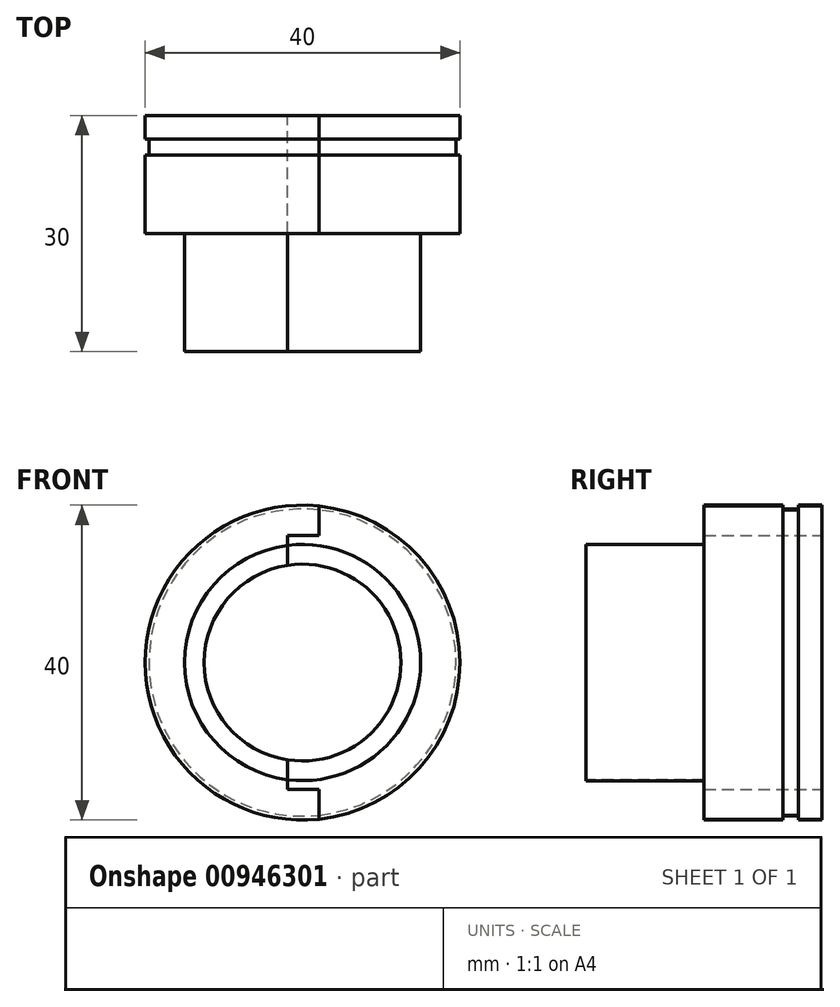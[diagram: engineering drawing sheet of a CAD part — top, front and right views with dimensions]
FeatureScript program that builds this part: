
annotation { "Feature Type Name" : "Feature", "Feature Type Description" : "" }
export const myFeature = defineFeature(function(context is Context, id is Id, definition is map)
    precondition{}
    {
        {
            var Q0;
            Q0=qCreatedBy(makeId("Front.planeOp"),FACE);
            var sketch = newSketch(context, id + "F0", { "sketchPlane" : qUnion([Q0])});
            skCircle(sketch, "E0", {"center": v(0, 0) * mm, "radius": 12.5 * mm});
            skCircle(sketch, "E1", {"center": v(0, 0) * mm, "radius": 15 * mm});
            skCircle(sketch, "E2", {"center": v(0, 0) * mm, "radius": 20 * mm});
            skSolve(sketch);
        }
        {
            var Q0;
            Q0=makeQuery(id+"F0.imprint","IMPRINT",FACE,{"disambiguationData":[TD([[makeQuery(id+"F0.imprint","IMPRINT",EDGE,{"derivedFrom":sQuery(id+"F0.wireOp",EDGE,"E0")}),-1.0]])]});
            extrude(context, id + "F1", {"entities" : qUnion([Q0]), "depth" : 30 * mm, "offsetDistance" : 25 * mm});
        }
        {
            var Q0;
            Q0 = qSketchRegion(id + "F0", true);
            extrude(context, id + "F2", {"entities" : qUnion([Q0]), "operationType" : NewBodyOperationType.ADD, "depth" : 30 * mm, "offsetDistance" : 25 * mm});
        }
        {
            var Q0;
            {var subQ0=sQuery(id+"F0.wireOp",EDGE,"E1");Q0=makeQuery(id+"F2.boolean.opBoolean","MERGE",FACE,{"derivedFrom":[makeQuery(id+"F1.opExtrude","CAP_FACE",FACE,{"disambiguationData":[OSD([sQuery(id+"F0.wireOp",EDGE,"E0"),subQ0])],"isStart":true}),makeQuery(id+"F2.opExtrude","CAP_FACE",FACE,{"disambiguationData":[OSD([subQ0,sQuery(id+"F0.wireOp",EDGE,"E2")])],"isStart":true})]});}
            var sketch = newSketch(context, id + "F3", { "sketchPlane" : qUnion([Q0])});
            skLineSegment(sketch, "E3", {"start": v(0, 27.45) * mm, "end": v(0, -30.32) * mm, "construction": true});
            skLineSegment(sketch, "E4", {"start": v(-35.74, 0) * mm, "end": v(39.77, 0) * mm, "construction": true});
            skLineSegment(sketch, "E5", {"start": v(-2.08, 19.9) * mm, "end": v(-2.08, 16.12) * mm});
            skLineSegment(sketch, "E6", {"start": v(-2.08, 16.12) * mm, "end": v(1.92, 16.12) * mm});
            skLineSegment(sketch, "E7", {"start": v(1.92, 16.12) * mm, "end": v(1.92, 12.35) * mm});
            skLineSegment(sketch, "E8.MirrorCS", {"start": v(1.92, -16.12) * mm, "end": v(1.92, -12.35) * mm});
            skLineSegment(sketch, "E9.MirrorCS", {"start": v(-2.08, -19.9) * mm, "end": v(-2.08, -16.12) * mm});
            skLineSegment(sketch, "E10.MirrorCS", {"start": v(-2.08, -16.12) * mm, "end": v(1.92, -16.12) * mm});
            skSolve(sketch);
        }
        {
            var Q0;
            {var subQ2=sQuery(id+"F3.wireOp",EDGE,"E5");Q0=makeQuery(id+"F3.imprint","IMPRINT",FACE,{"disambiguationData":[TD([[makeQuery(id+"F3.imprint","IMPRINT",EDGE,{"derivedFrom":subQ2}),-1.0]])]});}
            var sketch = newSketch(context, id + "F4", { "sketchPlane" : qUnion([Q0])});
            skLineSegment(sketch, "E11", {"start": v(-19.9, -2) * mm, "end": v(-15.9, -2) * mm});
            skLineSegment(sketch, "E12", {"start": v(-15.9, -2) * mm, "end": v(-15.9, 2) * mm});
            skLineSegment(sketch, "E13", {"start": v(-15.9, 2) * mm, "end": v(-12.34, 2) * mm});
            skLineSegment(sketch, "E14", {"start": v(-12.34, 1.9) * mm, "end": v(-15.84, 1.9) * mm});
            skLineSegment(sketch, "E15", {"start": v(-15.84, 1.9) * mm, "end": v(-15.84, -2.1) * mm});
            skLineSegment(sketch, "E16", {"start": v(-15.84, -2.1) * mm, "end": v(-19.84, -2.1) * mm});
            skSolve(sketch);
        }
        {
            var Q0;
            {var subQ3=sQuery(id+"F4.wireOp",EDGE,"E11");Q0=makeQuery(id+"F4.imprint","IMPRINT",FACE,{"disambiguationData":[TD([[makeQuery(id+"F4.imprint","IMPRINT",EDGE,{"derivedFrom":subQ3}),1.0]])]});}
            var Q1;
            {var subQ7=sQuery(id+"F4.wireOp",EDGE,"E11");Q1=makeQuery(id+"F4.imprint","IMPRINT",FACE,{"disambiguationData":[TD([[makeQuery(id+"F4.imprint","IMPRINT",EDGE,{"derivedFrom":subQ7}),-1.0]])]});}
            extrude(context, id + "F5", {"entities" : qUnion([Q0, Q1]), "operationType" : NewBodyOperationType.REMOVE, "endBound" : BoundingType.THROUGH_ALL, "oppositeDirection" : true, "depth" : 25 * mm, "offsetDistance" : 25 * mm});
        }
        {
            var Q0;
            {var subQ2=sQuery(id+"F3.wireOp",EDGE,"E5");Q0=makeQuery(id+"F3.imprint","IMPRINT",FACE,{"disambiguationData":[TD([[makeQuery(id+"F3.imprint","IMPRINT",EDGE,{"derivedFrom":subQ2}),-1.0]])]});}
            extrude(context, id + "F6", {"entities" : qUnion([Q0]), "oppositeDirection" : true, "depth" : 30 * mm, "offsetDistance" : 25 * mm});
        }
        {
            var Q0;
            {var subQ0=sQuery(id+"F0.wireOp",EDGE,"E1");Q0=makeQuery(id+"F2.boolean.opBoolean","MERGE",FACE,{"derivedFrom":[makeQuery(id+"F1.opExtrude","CAP_FACE",FACE,{"disambiguationData":[OSD([sQuery(id+"F0.wireOp",EDGE,"E0"),subQ0])],"isStart":false}),makeQuery(id+"F2.opExtrude","CAP_FACE",FACE,{"disambiguationData":[OSD([subQ0,sQuery(id+"F0.wireOp",EDGE,"E2")])],"isStart":false})]});}
            var sketch = newSketch(context, id + "F7", { "sketchPlane" : qUnion([Q0])});
            skCircle(sketch, "E17", {"center": v(0, 0) * mm, "radius": 15 * mm});
            skSolve(sketch);
        }
        {
            var Q0;
            {var subQ0=sQuery(id+"F0.wireOp",EDGE,"E2");Q0=makeQuery(id+"F7.imprint","IMPRINT",FACE,{"disambiguationData":[TD([[makeQuery(id+"F7.imprint","IMPRINT",EDGE,{"derivedFrom":makeQuery(id+"F2.opExtrude","CAP_EDGE",EDGE,{"disambiguationData":[OSD([subQ0])],"isStart":false})}),1.0]])]});}
            extrude(context, id + "F8", {"entities" : qUnion([Q0]), "operationType" : NewBodyOperationType.REMOVE, "oppositeDirection" : true, "depth" : 15 * mm, "offsetDistance" : 25 * mm});
        }
        {
            var Q0;
            Q0=makeQuery(id+"F6.opExtrude","CAP_FACE",FACE,{"disambiguationData":[OSD([sQuery(id+"F0.wireOp",EDGE,"E0"),sQuery(id+"F0.wireOp",EDGE,"E2"),sQuery(id+"F3.wireOp",EDGE,"E5"),sQuery(id+"F3.wireOp",EDGE,"E6"),sQuery(id+"F3.wireOp",EDGE,"E7"),sQuery(id+"F3.wireOp",EDGE,"E8.MirrorCS"),sQuery(id+"F3.wireOp",EDGE,"E9.MirrorCS"),sQuery(id+"F3.wireOp",EDGE,"E10.MirrorCS")])],"isStart":false});
            var sketch = newSketch(context, id + "F9", { "sketchPlane" : qUnion([Q0])});
            skCircle(sketch, "E18", {"center": v(0, 0) * mm, "radius": 15 * mm});
            skSolve(sketch);
        }
        {
            var Q0;
            Q0=makeQuery(id+"F9.imprint","IMPRINT",FACE,{"disambiguationData":[TD([[makeQuery(id+"F9.imprint","IMPRINT",EDGE,{"derivedFrom":makeQuery(id+"F6.opExtrude","CAP_EDGE",EDGE,{"disambiguationData":[OSD([sQuery(id+"F3.wireOp",EDGE,"E5")])],"isStart":false})}),1.0]])]});
            extrude(context, id + "F10", {"entities" : qUnion([Q0]), "operationType" : NewBodyOperationType.REMOVE, "oppositeDirection" : true, "depth" : 15 * mm, "offsetDistance" : 25 * mm});
        }
        {
            var Q0;
            Q0=makeQuery(id+"F6.opExtrude","CAP_FACE",FACE,{"disambiguationData":[OSD([sQuery(id+"F0.wireOp",EDGE,"E0"),sQuery(id+"F0.wireOp",EDGE,"E2"),sQuery(id+"F3.wireOp",EDGE,"E5"),sQuery(id+"F3.wireOp",EDGE,"E6"),sQuery(id+"F3.wireOp",EDGE,"E7"),sQuery(id+"F3.wireOp",EDGE,"E8.MirrorCS"),sQuery(id+"F3.wireOp",EDGE,"E9.MirrorCS"),sQuery(id+"F3.wireOp",EDGE,"E10.MirrorCS")])],"isStart":true});
            var sketch = newSketch(context, id + "F11", { "sketchPlane" : qUnion([Q0])});
            skCircle(sketch, "E19", {"center": v(0, 0) * mm, "radius": 19.5 * mm});
            skSolve(sketch);
        }
        {
            var Q0;
            {var subQ5=makeQuery(id+"F6.opExtrude","CAP_EDGE",EDGE,{"disambiguationData":[OSD([sQuery(id+"F0.wireOp",EDGE,"E2")])],"isStart":true});Q0=makeQuery(id+"F11.imprint","IMPRINT",FACE,{"disambiguationData":[TD([[makeQuery(id+"F11.imprint","IMPRINT",EDGE,{"derivedFrom":subQ5}),-1.0]])]});}
            extrude(context, id + "F12", {"entities" : qUnion([Q0]), "operationType" : NewBodyOperationType.REMOVE, "oppositeDirection" : true, "depth" : 5 * mm, "offsetDistance" : 25 * mm, "hasSecondDirection" : true, "secondDirectionOppositeDirection" : true, "secondDirectionDepth" : 3 * mm});
        }
        {
            var Q0;
            {var subQ0=sQuery(id+"F0.wireOp",EDGE,"E1");Q0=makeQuery(id+"F2.boolean.opBoolean","MERGE",FACE,{"derivedFrom":[makeQuery(id+"F1.opExtrude","CAP_FACE",FACE,{"disambiguationData":[OSD([sQuery(id+"F0.wireOp",EDGE,"E0"),subQ0])],"isStart":true}),makeQuery(id+"F2.opExtrude","CAP_FACE",FACE,{"disambiguationData":[OSD([subQ0,sQuery(id+"F0.wireOp",EDGE,"E2")])],"isStart":true})]});}
            var sketch = newSketch(context, id + "F13", { "sketchPlane" : qUnion([Q0])});
            skCircle(sketch, "E20", {"center": v(0, 0) * mm, "radius": 19.5 * mm});
            skSolve(sketch);
        }
        {
            var Q0;
            {var subQ5=makeQuery(id+"F2.opExtrude","CAP_EDGE",EDGE,{"disambiguationData":[OSD([sQuery(id+"F0.wireOp",EDGE,"E2")])],"isStart":true});Q0=makeQuery(id+"F13.imprint","IMPRINT",FACE,{"disambiguationData":[TD([[makeQuery(id+"F13.imprint","IMPRINT",EDGE,{"derivedFrom":subQ5}),-1.0]])]});}
            extrude(context, id + "F14", {"entities" : qUnion([Q0]), "operationType" : NewBodyOperationType.REMOVE, "oppositeDirection" : true, "depth" : 5 * mm, "offsetDistance" : 25 * mm, "hasSecondDirection" : true, "secondDirectionOppositeDirection" : true, "secondDirectionDepth" : 3 * mm});
        }
    });
